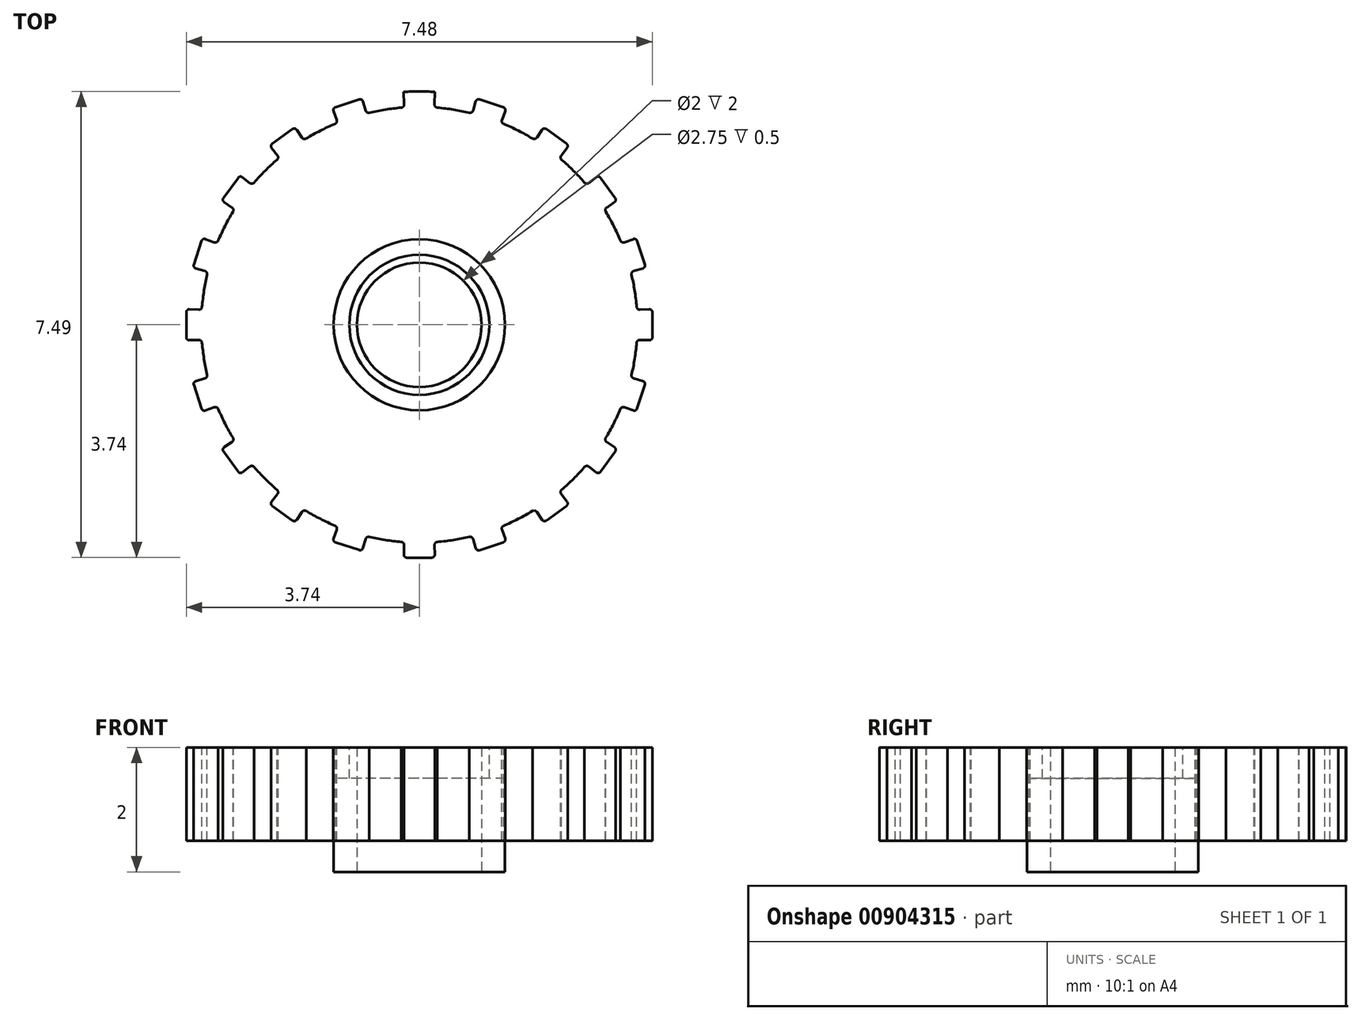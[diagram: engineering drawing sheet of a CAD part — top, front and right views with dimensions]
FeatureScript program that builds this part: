
annotation { "Feature Type Name" : "Feature", "Feature Type Description" : "" }
export const myFeature = defineFeature(function(context is Context, id is Id, definition is map)
    precondition{}
    {
        {
            var Q0;
            Q0=qCreatedBy(makeId("Front.planeOp"),FACE);
            var sketch = newSketch(context, id + "F0", { "sketchPlane" : qUnion([Q0])});
            skLineSegment(sketch, "E0.bottom", {"start": v(0, 0) * mm, "end": v(-3.75, 0) * mm});
            skLineSegment(sketch, "E0.top", {"start": v(0, 2) * mm, "end": v(-3.75, 2) * mm});
            skLineSegment(sketch, "E0.left", {"start": v(0, 0) * mm, "end": v(0, 2) * mm});
            skLineSegment(sketch, "E0.right", {"start": v(-3.75, 0) * mm, "end": v(-3.75, 2) * mm});
            skLineSegment(sketch, "E1", {"start": v(-1, 2) * mm, "end": v(-1, 0) * mm});
            skSolve(sketch);
        }
        {
            var Q0;
            {var subQ0=sQuery(id+"F0.wireOp",EDGE,"E0.right");Q0=makeQuery(id+"F0.imprint","IMPRINT",FACE,{"disambiguationData":[TD([[makeQuery(id+"F0.imprint","IMPRINT",EDGE,{"derivedFrom":subQ0}),-1.0]])]});}
            var Q1;
            Q1=sQuery(id+"F0.wireOp",EDGE,"E0.left");
            revolve(context, id + "F1", {"surfaceOperationType" : NewSurfaceOperationType.NEW, "entities" : qUnion([Q0]), "axis" : qUnion([Q1]), "revolveType" : RevolveType.FULL});
        }
        {
            var Q0;
            Q0=makeQuery(id+"F1.opRevolve","SWEPT_FACE",FACE,{"disambiguationData":[OSD([sQuery(id+"F0.wireOp",EDGE,"E0.top")])]});
            var sketch = newSketch(context, id + "F2", { "sketchPlane" : qUnion([Q0])});
            skLineSegment(sketch, "E2", {"start": v(0, 0) * mm, "end": v(0, 3.75) * mm});
            skLineSegment(sketch, "E3", {"start": v(0, 3.74) * mm, "end": v(-0.25, 3.74) * mm});
            skLineSegment(sketch, "E4", {"start": v(-0.25, 3.74) * mm, "end": v(0.25, 3.74) * mm});
            skLineSegment(sketch, "E5.bottom", {"start": v(0.12, 0) * mm, "end": v(-0.12, 0) * mm});
            skLineSegment(sketch, "E5.top", {"start": v(0.12, 0) * mm, "end": v(-0.12, 0) * mm});
            skLineSegment(sketch, "E5.left", {"start": v(0.12, 0) * mm, "end": v(0.12, 0) * mm});
            skLineSegment(sketch, "E5.right", {"start": v(-0.12, 0) * mm, "end": v(-0.12, 0) * mm});
            skPoint(sketch, "E5.middle", {"position": v(0, 0) * mm});
            skLineSegment(sketch, "E6", {"start": v(-0.25, 3.74) * mm, "end": v(-0.13, 0) * mm});
            skLineSegment(sketch, "E7", {"start": v(0.25, 3.74) * mm, "end": v(0.12, 0) * mm});
            skCircle(sketch, "E8", {"center": v(0, 0) * mm, "radius": 3.5 * mm});
            skLineSegment(sketch, "E9", {"start": v(-0.25, 3.74) * mm, "end": v(-0.2, 3.74) * mm});
            skLineSegment(sketch, "E10", {"start": v(-0.2, 3.74) * mm, "end": v(0.2, 3.74) * mm});
            skLineSegment(sketch, "E11", {"start": v(0.2, 3.74) * mm, "end": v(0.25, 3.74) * mm});
            skLineSegment(sketch, "E12", {"start": v(-0.2, 3.74) * mm, "end": v(-0.12, 0) * mm});
            skLineSegment(sketch, "E13", {"start": v(0.2, 3.74) * mm, "end": v(0.12, 0) * mm});
            skLineSegment(sketch, "E14", {"start": v(-0.25, 3.7) * mm, "end": v(0.25, 3.7) * mm});
            skLineSegment(sketch, "E15", {"start": v(-0.25, 3.7) * mm, "end": v(-0.3, 3.7) * mm});
            skLineSegment(sketch, "E16", {"start": v(0.25, 3.7) * mm, "end": v(0.3, 3.7) * mm});
            skLineSegment(sketch, "E17", {"start": v(-0.3, 3.7) * mm, "end": v(-0.13, 0) * mm});
            skLineSegment(sketch, "E18", {"start": v(0.3, 3.7) * mm, "end": v(0.13, 0) * mm});
            skLineSegment(sketch, "E19", {"start": v(-0.24, 3.54) * mm, "end": v(0.2, 3.54) * mm});
            skLineSegment(sketch, "E20", {"start": v(0.2, 3.54) * mm, "end": v(0.24, 3.54) * mm});
            skLineSegment(sketch, "E21", {"start": v(0.24, 3.54) * mm, "end": v(-0.2, 3.54) * mm});
            skArc(sketch, "E22", {"start": v(-0.29, 3.49) * mm, "mid": v(-0.26, 3.5) * mm, "end": v(-0.24, 3.54) * mm});
            skArc(sketch, "E23", {"start": v(-0.2, 3.74) * mm, "mid": v(-0.23, 3.73) * mm, "end": v(-0.25, 3.7) * mm});
            skArc(sketch, "E24", {"start": v(0.25, 3.7) * mm, "mid": v(0.23, 3.73) * mm, "end": v(0.2, 3.74) * mm});
            skArc(sketch, "E25", {"start": v(0.24, 3.54) * mm, "mid": v(0.26, 3.5) * mm, "end": v(0.29, 3.49) * mm});
            skArc(sketch, "E26.1.0", {"start": v(-1.35, 3.23) * mm, "mid": v(-1.33, 3.26) * mm, "end": v(-1.33, 3.3) * mm});
            skLineSegment(sketch, "E26.1.1", {"start": v(-1.4, 3.48) * mm, "end": v(-0.12, -0.04) * mm});
            skArc(sketch, "E26.1.2", {"start": v(-1.35, 3.5) * mm, "mid": v(-1.37, 3.47) * mm, "end": v(-1.38, 3.43) * mm});
            skLineSegment(sketch, "E26.1.3", {"start": v(-1.4, 3.48) * mm, "end": v(-0.92, 3.64) * mm});
            skArc(sketch, "E26.1.4", {"start": v(-0.9, 3.59) * mm, "mid": v(-0.93, 3.62) * mm, "end": v(-0.97, 3.62) * mm});
            skLineSegment(sketch, "E26.1.5", {"start": v(-0.92, 3.64) * mm, "end": v(0.12, 0.04) * mm});
            skArc(sketch, "E26.1.6", {"start": v(-0.86, 3.44) * mm, "mid": v(-0.84, 3.41) * mm, "end": v(-0.8, 3.4) * mm});
            skArc(sketch, "E26.2.0", {"start": v(-2.28, 2.65) * mm, "mid": v(-2.27, 2.69) * mm, "end": v(-2.28, 2.72) * mm});
            skLineSegment(sketch, "E26.2.1", {"start": v(-2.4, 2.88) * mm, "end": v(-0.1, -0.07) * mm});
            skArc(sketch, "E26.2.2", {"start": v(-2.36, 2.9) * mm, "mid": v(-2.38, 2.88) * mm, "end": v(-2.37, 2.84) * mm});
            skLineSegment(sketch, "E26.2.3", {"start": v(-2.4, 2.88) * mm, "end": v(-2, 3.17) * mm});
            skArc(sketch, "E26.2.4", {"start": v(-1.97, 3.13) * mm, "mid": v(-2, 3.15) * mm, "end": v(-2.04, 3.14) * mm});
            skLineSegment(sketch, "E26.2.5", {"start": v(-2, 3.17) * mm, "end": v(0.1, 0.07) * mm});
            skArc(sketch, "E26.2.6", {"start": v(-1.88, 3) * mm, "mid": v(-1.85, 2.99) * mm, "end": v(-1.82, 3) * mm});
            skArc(sketch, "E27.2.3.0", {"start": v(-3, 1.82) * mm, "mid": v(-2.99, 1.85) * mm, "end": v(-3, 1.88) * mm});
            skLineSegment(sketch, "E27.4.3.0", {"start": v(-3.17, 2) * mm, "end": v(-0.07, -0.1) * mm});
            skArc(sketch, "E27.7.3.0", {"start": v(-3.14, 2.04) * mm, "mid": v(-3.15, 2) * mm, "end": v(-3.13, 1.97) * mm});
            skLineSegment(sketch, "E27.11.3.0", {"start": v(-3.17, 2) * mm, "end": v(-2.88, 2.4) * mm});
            skArc(sketch, "E27.14.3.0", {"start": v(-2.84, 2.37) * mm, "mid": v(-2.88, 2.38) * mm, "end": v(-2.9, 2.36) * mm});
            skLineSegment(sketch, "E27.18.3.0", {"start": v(-2.88, 2.4) * mm, "end": v(0.07, 0.1) * mm});
            skArc(sketch, "E27.21.3.0", {"start": v(-2.72, 2.28) * mm, "mid": v(-2.69, 2.27) * mm, "end": v(-2.65, 2.28) * mm});
            skArc(sketch, "E27.2.4.0", {"start": v(-3.4, 0.8) * mm, "mid": v(-3.41, 0.84) * mm, "end": v(-3.44, 0.86) * mm});
            skLineSegment(sketch, "E27.4.4.0", {"start": v(-3.64, 0.92) * mm, "end": v(-0.04, -0.12) * mm});
            skArc(sketch, "E27.7.4.0", {"start": v(-3.62, 0.97) * mm, "mid": v(-3.62, 0.93) * mm, "end": v(-3.59, 0.9) * mm});
            skLineSegment(sketch, "E27.11.4.0", {"start": v(-3.64, 0.92) * mm, "end": v(-3.48, 1.4) * mm});
            skArc(sketch, "E27.14.4.0", {"start": v(-3.43, 1.38) * mm, "mid": v(-3.47, 1.37) * mm, "end": v(-3.5, 1.35) * mm});
            skLineSegment(sketch, "E27.18.4.0", {"start": v(-3.48, 1.4) * mm, "end": v(0.04, 0.12) * mm});
            skArc(sketch, "E27.21.4.0", {"start": v(-3.3, 1.33) * mm, "mid": v(-3.26, 1.33) * mm, "end": v(-3.23, 1.35) * mm});
            skArc(sketch, "E27.2.5.0", {"start": v(-3.49, -0.29) * mm, "mid": v(-3.5, -0.26) * mm, "end": v(-3.54, -0.24) * mm});
            skLineSegment(sketch, "E27.4.5.0", {"start": v(-3.74, -0.25) * mm, "end": v(0, -0.12) * mm});
            skArc(sketch, "E27.7.5.0", {"start": v(-3.74, -0.2) * mm, "mid": v(-3.73, -0.23) * mm, "end": v(-3.7, -0.25) * mm});
            skLineSegment(sketch, "E27.11.5.0", {"start": v(-3.74, -0.25) * mm, "end": v(-3.74, 0.25) * mm});
            skArc(sketch, "E27.14.5.0", {"start": v(-3.7, 0.25) * mm, "mid": v(-3.73, 0.23) * mm, "end": v(-3.74, 0.2) * mm});
            skLineSegment(sketch, "E27.18.5.0", {"start": v(-3.74, 0.25) * mm, "end": v(0, 0.13) * mm});
            skArc(sketch, "E27.21.5.0", {"start": v(-3.54, 0.24) * mm, "mid": v(-3.5, 0.26) * mm, "end": v(-3.49, 0.29) * mm});
            skArc(sketch, "E27.2.6.0", {"start": v(-3.23, -1.35) * mm, "mid": v(-3.26, -1.33) * mm, "end": v(-3.3, -1.33) * mm});
            skLineSegment(sketch, "E27.4.6.0", {"start": v(-3.48, -1.4) * mm, "end": v(0.04, -0.12) * mm});
            skArc(sketch, "E27.7.6.0", {"start": v(-3.5, -1.35) * mm, "mid": v(-3.47, -1.37) * mm, "end": v(-3.43, -1.38) * mm});
            skLineSegment(sketch, "E27.11.6.0", {"start": v(-3.48, -1.4) * mm, "end": v(-3.64, -0.92) * mm});
            skArc(sketch, "E27.14.6.0", {"start": v(-3.59, -0.9) * mm, "mid": v(-3.62, -0.93) * mm, "end": v(-3.62, -0.97) * mm});
            skLineSegment(sketch, "E27.18.6.0", {"start": v(-3.64, -0.92) * mm, "end": v(-0.04, 0.12) * mm});
            skArc(sketch, "E27.21.6.0", {"start": v(-3.44, -0.86) * mm, "mid": v(-3.41, -0.84) * mm, "end": v(-3.4, -0.8) * mm});
            skArc(sketch, "E27.2.7.0", {"start": v(-2.65, -2.28) * mm, "mid": v(-2.69, -2.27) * mm, "end": v(-2.72, -2.28) * mm});
            skLineSegment(sketch, "E27.4.7.0", {"start": v(-2.88, -2.4) * mm, "end": v(0.07, -0.1) * mm});
            skArc(sketch, "E27.7.7.0", {"start": v(-2.9, -2.36) * mm, "mid": v(-2.88, -2.38) * mm, "end": v(-2.84, -2.37) * mm});
            skLineSegment(sketch, "E27.11.7.0", {"start": v(-2.88, -2.4) * mm, "end": v(-3.17, -2) * mm});
            skArc(sketch, "E27.14.7.0", {"start": v(-3.13, -1.97) * mm, "mid": v(-3.15, -2) * mm, "end": v(-3.14, -2.04) * mm});
            skLineSegment(sketch, "E27.18.7.0", {"start": v(-3.17, -2) * mm, "end": v(-0.07, 0.1) * mm});
            skArc(sketch, "E27.21.7.0", {"start": v(-3, -1.88) * mm, "mid": v(-2.99, -1.85) * mm, "end": v(-3, -1.82) * mm});
            skArc(sketch, "E28.2.8.0", {"start": v(-1.82, -3) * mm, "mid": v(-1.85, -2.99) * mm, "end": v(-1.88, -3) * mm});
            skLineSegment(sketch, "E28.4.8.0", {"start": v(-2, -3.17) * mm, "end": v(0.1, -0.07) * mm});
            skArc(sketch, "E28.7.8.0", {"start": v(-2.04, -3.14) * mm, "mid": v(-2, -3.15) * mm, "end": v(-1.97, -3.13) * mm});
            skLineSegment(sketch, "E28.11.8.0", {"start": v(-2, -3.17) * mm, "end": v(-2.4, -2.88) * mm});
            skArc(sketch, "E28.14.8.0", {"start": v(-2.37, -2.84) * mm, "mid": v(-2.38, -2.88) * mm, "end": v(-2.36, -2.9) * mm});
            skLineSegment(sketch, "E28.18.8.0", {"start": v(-2.4, -2.88) * mm, "end": v(-0.1, 0.07) * mm});
            skArc(sketch, "E28.21.8.0", {"start": v(-2.28, -2.72) * mm, "mid": v(-2.27, -2.69) * mm, "end": v(-2.28, -2.65) * mm});
            skArc(sketch, "E28.2.9.0", {"start": v(-0.8, -3.4) * mm, "mid": v(-0.84, -3.41) * mm, "end": v(-0.86, -3.44) * mm});
            skLineSegment(sketch, "E28.4.9.0", {"start": v(-0.92, -3.64) * mm, "end": v(0.12, -0.04) * mm});
            skArc(sketch, "E28.7.9.0", {"start": v(-0.97, -3.62) * mm, "mid": v(-0.93, -3.62) * mm, "end": v(-0.9, -3.59) * mm});
            skLineSegment(sketch, "E28.11.9.0", {"start": v(-0.92, -3.64) * mm, "end": v(-1.4, -3.48) * mm});
            skArc(sketch, "E28.14.9.0", {"start": v(-1.38, -3.43) * mm, "mid": v(-1.37, -3.47) * mm, "end": v(-1.35, -3.5) * mm});
            skLineSegment(sketch, "E28.18.9.0", {"start": v(-1.4, -3.48) * mm, "end": v(-0.12, 0.04) * mm});
            skArc(sketch, "E28.21.9.0", {"start": v(-1.33, -3.3) * mm, "mid": v(-1.33, -3.26) * mm, "end": v(-1.35, -3.23) * mm});
            skArc(sketch, "E28.2.10.0", {"start": v(0.29, -3.49) * mm, "mid": v(0.26, -3.5) * mm, "end": v(0.24, -3.54) * mm});
            skLineSegment(sketch, "E28.4.10.0", {"start": v(0.25, -3.74) * mm, "end": v(0.13, 0) * mm});
            skArc(sketch, "E28.7.10.0", {"start": v(0.2, -3.74) * mm, "mid": v(0.23, -3.73) * mm, "end": v(0.25, -3.7) * mm});
            skLineSegment(sketch, "E28.11.10.0", {"start": v(0.25, -3.74) * mm, "end": v(-0.25, -3.74) * mm});
            skArc(sketch, "E28.14.10.0", {"start": v(-0.25, -3.7) * mm, "mid": v(-0.23, -3.73) * mm, "end": v(-0.2, -3.74) * mm});
            skLineSegment(sketch, "E28.18.10.0", {"start": v(-0.25, -3.74) * mm, "end": v(-0.12, 0) * mm});
            skArc(sketch, "E28.21.10.0", {"start": v(-0.24, -3.54) * mm, "mid": v(-0.26, -3.5) * mm, "end": v(-0.29, -3.49) * mm});
            skArc(sketch, "E28.2.11.0", {"start": v(1.35, -3.23) * mm, "mid": v(1.33, -3.26) * mm, "end": v(1.33, -3.3) * mm});
            skLineSegment(sketch, "E28.4.11.0", {"start": v(1.4, -3.48) * mm, "end": v(0.12, 0.04) * mm});
            skArc(sketch, "E28.7.11.0", {"start": v(1.35, -3.5) * mm, "mid": v(1.37, -3.47) * mm, "end": v(1.38, -3.43) * mm});
            skLineSegment(sketch, "E28.11.11.0", {"start": v(1.4, -3.48) * mm, "end": v(0.92, -3.64) * mm});
            skArc(sketch, "E28.14.11.0", {"start": v(0.9, -3.59) * mm, "mid": v(0.93, -3.62) * mm, "end": v(0.97, -3.62) * mm});
            skLineSegment(sketch, "E28.18.11.0", {"start": v(0.92, -3.64) * mm, "end": v(-0.12, -0.04) * mm});
            skArc(sketch, "E28.21.11.0", {"start": v(0.86, -3.44) * mm, "mid": v(0.84, -3.41) * mm, "end": v(0.8, -3.4) * mm});
            skArc(sketch, "E28.2.12.0", {"start": v(2.28, -2.65) * mm, "mid": v(2.27, -2.69) * mm, "end": v(2.28, -2.72) * mm});
            skLineSegment(sketch, "E28.4.12.0", {"start": v(2.4, -2.88) * mm, "end": v(0.1, 0.07) * mm});
            skArc(sketch, "E28.7.12.0", {"start": v(2.36, -2.9) * mm, "mid": v(2.38, -2.88) * mm, "end": v(2.37, -2.84) * mm});
            skLineSegment(sketch, "E28.11.12.0", {"start": v(2.4, -2.88) * mm, "end": v(2, -3.17) * mm});
            skArc(sketch, "E28.14.12.0", {"start": v(1.97, -3.13) * mm, "mid": v(2, -3.15) * mm, "end": v(2.04, -3.14) * mm});
            skLineSegment(sketch, "E28.18.12.0", {"start": v(2, -3.17) * mm, "end": v(-0.1, -0.07) * mm});
            skArc(sketch, "E28.21.12.0", {"start": v(1.88, -3) * mm, "mid": v(1.85, -2.99) * mm, "end": v(1.82, -3) * mm});
            skArc(sketch, "E28.2.13.0", {"start": v(3, -1.82) * mm, "mid": v(2.99, -1.85) * mm, "end": v(3, -1.88) * mm});
            skLineSegment(sketch, "E28.4.13.0", {"start": v(3.17, -2) * mm, "end": v(0.07, 0.1) * mm});
            skArc(sketch, "E28.7.13.0", {"start": v(3.14, -2.04) * mm, "mid": v(3.15, -2) * mm, "end": v(3.13, -1.97) * mm});
            skLineSegment(sketch, "E28.11.13.0", {"start": v(3.17, -2) * mm, "end": v(2.88, -2.4) * mm});
            skArc(sketch, "E28.14.13.0", {"start": v(2.84, -2.37) * mm, "mid": v(2.88, -2.38) * mm, "end": v(2.9, -2.36) * mm});
            skLineSegment(sketch, "E28.18.13.0", {"start": v(2.88, -2.4) * mm, "end": v(-0.07, -0.1) * mm});
            skArc(sketch, "E28.21.13.0", {"start": v(2.72, -2.28) * mm, "mid": v(2.69, -2.27) * mm, "end": v(2.65, -2.28) * mm});
            skArc(sketch, "E29.2.14.0", {"start": v(3.4, -0.8) * mm, "mid": v(3.41, -0.84) * mm, "end": v(3.44, -0.86) * mm});
            skLineSegment(sketch, "E29.4.14.0", {"start": v(3.64, -0.92) * mm, "end": v(0.04, 0.12) * mm});
            skArc(sketch, "E29.7.14.0", {"start": v(3.62, -0.97) * mm, "mid": v(3.62, -0.93) * mm, "end": v(3.59, -0.9) * mm});
            skLineSegment(sketch, "E29.11.14.0", {"start": v(3.64, -0.92) * mm, "end": v(3.48, -1.4) * mm});
            skArc(sketch, "E29.14.14.0", {"start": v(3.43, -1.38) * mm, "mid": v(3.47, -1.37) * mm, "end": v(3.5, -1.35) * mm});
            skLineSegment(sketch, "E29.18.14.0", {"start": v(3.48, -1.4) * mm, "end": v(-0.04, -0.12) * mm});
            skArc(sketch, "E29.21.14.0", {"start": v(3.3, -1.33) * mm, "mid": v(3.26, -1.33) * mm, "end": v(3.23, -1.35) * mm});
            skArc(sketch, "E29.2.15.0", {"start": v(3.49, 0.29) * mm, "mid": v(3.5, 0.26) * mm, "end": v(3.54, 0.24) * mm});
            skLineSegment(sketch, "E29.4.15.0", {"start": v(3.74, 0.25) * mm, "end": v(0, 0.12) * mm});
            skArc(sketch, "E29.7.15.0", {"start": v(3.74, 0.2) * mm, "mid": v(3.73, 0.23) * mm, "end": v(3.7, 0.25) * mm});
            skLineSegment(sketch, "E29.11.15.0", {"start": v(3.74, 0.25) * mm, "end": v(3.74, -0.25) * mm});
            skArc(sketch, "E29.14.15.0", {"start": v(3.7, -0.25) * mm, "mid": v(3.73, -0.23) * mm, "end": v(3.74, -0.2) * mm});
            skLineSegment(sketch, "E29.18.15.0", {"start": v(3.74, -0.25) * mm, "end": v(0, -0.13) * mm});
            skArc(sketch, "E29.21.15.0", {"start": v(3.54, -0.24) * mm, "mid": v(3.5, -0.26) * mm, "end": v(3.49, -0.29) * mm});
            skArc(sketch, "E30.2.16.0", {"start": v(3.23, 1.35) * mm, "mid": v(3.26, 1.33) * mm, "end": v(3.3, 1.33) * mm});
            skLineSegment(sketch, "E30.4.16.0", {"start": v(3.48, 1.4) * mm, "end": v(-0.04, 0.12) * mm});
            skArc(sketch, "E30.7.16.0", {"start": v(3.5, 1.35) * mm, "mid": v(3.47, 1.37) * mm, "end": v(3.43, 1.38) * mm});
            skLineSegment(sketch, "E30.11.16.0", {"start": v(3.48, 1.4) * mm, "end": v(3.64, 0.92) * mm});
            skArc(sketch, "E30.14.16.0", {"start": v(3.59, 0.9) * mm, "mid": v(3.62, 0.93) * mm, "end": v(3.62, 0.97) * mm});
            skLineSegment(sketch, "E30.18.16.0", {"start": v(3.64, 0.92) * mm, "end": v(0.04, -0.12) * mm});
            skArc(sketch, "E30.21.16.0", {"start": v(3.44, 0.86) * mm, "mid": v(3.41, 0.84) * mm, "end": v(3.4, 0.8) * mm});
            skArc(sketch, "E30.2.17.0", {"start": v(2.65, 2.28) * mm, "mid": v(2.69, 2.27) * mm, "end": v(2.72, 2.28) * mm});
            skLineSegment(sketch, "E30.4.17.0", {"start": v(2.88, 2.4) * mm, "end": v(-0.07, 0.1) * mm});
            skArc(sketch, "E30.7.17.0", {"start": v(2.9, 2.36) * mm, "mid": v(2.88, 2.38) * mm, "end": v(2.84, 2.37) * mm});
            skLineSegment(sketch, "E30.11.17.0", {"start": v(2.88, 2.4) * mm, "end": v(3.17, 2) * mm});
            skArc(sketch, "E30.14.17.0", {"start": v(3.13, 1.97) * mm, "mid": v(3.15, 2) * mm, "end": v(3.14, 2.04) * mm});
            skLineSegment(sketch, "E30.18.17.0", {"start": v(3.17, 2) * mm, "end": v(0.07, -0.1) * mm});
            skArc(sketch, "E30.21.17.0", {"start": v(3, 1.88) * mm, "mid": v(2.99, 1.85) * mm, "end": v(3, 1.82) * mm});
            skArc(sketch, "E30.2.18.0", {"start": v(1.82, 3) * mm, "mid": v(1.85, 2.99) * mm, "end": v(1.88, 3) * mm});
            skLineSegment(sketch, "E30.4.18.0", {"start": v(2, 3.17) * mm, "end": v(-0.1, 0.07) * mm});
            skArc(sketch, "E30.7.18.0", {"start": v(2.04, 3.14) * mm, "mid": v(2, 3.15) * mm, "end": v(1.97, 3.13) * mm});
            skLineSegment(sketch, "E30.11.18.0", {"start": v(2, 3.17) * mm, "end": v(2.4, 2.88) * mm});
            skArc(sketch, "E30.14.18.0", {"start": v(2.37, 2.84) * mm, "mid": v(2.38, 2.88) * mm, "end": v(2.36, 2.9) * mm});
            skLineSegment(sketch, "E30.18.18.0", {"start": v(2.4, 2.88) * mm, "end": v(0.1, -0.07) * mm});
            skArc(sketch, "E30.21.18.0", {"start": v(2.28, 2.72) * mm, "mid": v(2.27, 2.69) * mm, "end": v(2.28, 2.65) * mm});
            skArc(sketch, "E30.2.19.0", {"start": v(0.8, 3.4) * mm, "mid": v(0.84, 3.41) * mm, "end": v(0.86, 3.44) * mm});
            skLineSegment(sketch, "E30.4.19.0", {"start": v(0.92, 3.64) * mm, "end": v(-0.12, 0.04) * mm});
            skArc(sketch, "E30.7.19.0", {"start": v(0.97, 3.62) * mm, "mid": v(0.93, 3.62) * mm, "end": v(0.9, 3.59) * mm});
            skLineSegment(sketch, "E30.11.19.0", {"start": v(0.92, 3.64) * mm, "end": v(1.4, 3.48) * mm});
            skArc(sketch, "E30.14.19.0", {"start": v(1.38, 3.43) * mm, "mid": v(1.37, 3.47) * mm, "end": v(1.35, 3.5) * mm});
            skLineSegment(sketch, "E30.18.19.0", {"start": v(1.4, 3.48) * mm, "end": v(0.12, -0.04) * mm});
            skArc(sketch, "E30.21.19.0", {"start": v(1.33, 3.3) * mm, "mid": v(1.33, 3.26) * mm, "end": v(1.35, 3.23) * mm});
            skSolve(sketch);
        }
        {
            var Q0;
            {var subQ1=sQuery(id+"F2.wireOp",EDGE,"E15");Q0=makeQuery(id+"F2.imprint","IMPRINT",FACE,{"disambiguationData":[TD([[makeQuery(id+"F2.imprint","IMPRINT",EDGE,{"derivedFrom":subQ1}),-1.0]])]});}
            var Q1;
            {var subQ0=sQuery(id+"F2.wireOp",EDGE,"E15");Q1=makeQuery(id+"F2.imprint","IMPRINT",FACE,{"disambiguationData":[TD([[makeQuery(id+"F2.imprint","IMPRINT",EDGE,{"derivedFrom":subQ0}),1.0]])]});}
            var Q2;
            {var subQ0=sQuery(id+"F2.wireOp",EDGE,"E9");Q2=makeQuery(id+"F2.imprint","IMPRINT",FACE,{"disambiguationData":[TD([[makeQuery(id+"F2.imprint","IMPRINT",EDGE,{"derivedFrom":subQ0}),-1.0]])]});}
            var Q3;
            {var subQ5=sQuery(id+"F2.wireOp",EDGE,"E9");Q3=makeQuery(id+"F2.imprint","IMPRINT",FACE,{"disambiguationData":[TD([[makeQuery(id+"F2.imprint","IMPRINT",EDGE,{"derivedFrom":subQ5}),1.0]])]});}
            var Q4;
            {var subQ5=sQuery(id+"F2.wireOp",EDGE,"E11");Q4=makeQuery(id+"F2.imprint","IMPRINT",FACE,{"disambiguationData":[TD([[makeQuery(id+"F2.imprint","IMPRINT",EDGE,{"derivedFrom":subQ5}),1.0]])]});}
            var Q5;
            {var subQ0=sQuery(id+"F2.wireOp",EDGE,"E11");Q5=makeQuery(id+"F2.imprint","IMPRINT",FACE,{"disambiguationData":[TD([[makeQuery(id+"F2.imprint","IMPRINT",EDGE,{"derivedFrom":subQ0}),-1.0]])]});}
            var Q6;
            {var subQ0=sQuery(id+"F2.wireOp",EDGE,"E16");Q6=makeQuery(id+"F2.imprint","IMPRINT",FACE,{"disambiguationData":[TD([[makeQuery(id+"F2.imprint","IMPRINT",EDGE,{"derivedFrom":subQ0}),1.0]])]});}
            var Q7;
            {var subQ0=sQuery(id+"F2.wireOp",EDGE,"E16");Q7=makeQuery(id+"F2.imprint","IMPRINT",FACE,{"disambiguationData":[TD([[makeQuery(id+"F2.imprint","IMPRINT",EDGE,{"derivedFrom":subQ0}),-1.0]])]});}
            var Q8;
            {var subQ3=sQuery(id+"F2.wireOp",EDGE,"E27.7.7.0");Q8=makeQuery(id+"F2.imprint","IMPRINT",FACE,{"disambiguationData":[TD([[makeQuery(id+"F2.imprint","IMPRINT",EDGE,{"derivedFrom":subQ3}),-1.0]])]});}
            var Q9;
            {var subQ0=sQuery(id+"F2.wireOp",EDGE,"E27.11.7.0");var subQ3=makeQuery(id+"F2.imprint","INTERSECT",VERTEX,{"derivedFrom":[sQuery(id+"F2.wireOp",EDGE,"E27.7.7.0"),subQ0]});Q9=makeQuery(id+"F2.imprint","IMPRINT",FACE,{"disambiguationData":[TD([[makeQuery(id+"F2.imprint","IMPRINT",EDGE,{"disambiguationData":[TD([[subQ3,-1.0]])],"derivedFrom":subQ0}),1.0]])]});}
            var Q10;
            {var subQ3=sQuery(id+"F2.wireOp",EDGE,"E27.14.7.0");Q10=makeQuery(id+"F2.imprint","IMPRINT",FACE,{"disambiguationData":[TD([[makeQuery(id+"F2.imprint","IMPRINT",EDGE,{"derivedFrom":subQ3}),-1.0]])]});}
            var Q11;
            {var subQ4=sQuery(id+"F2.wireOp",EDGE,"E27.2.6.0");Q11=makeQuery(id+"F2.imprint","IMPRINT",FACE,{"disambiguationData":[TD([[makeQuery(id+"F2.imprint","IMPRINT",EDGE,{"derivedFrom":subQ4}),1.0]])]});}
            var Q12;
            {var subQ3=sQuery(id+"F2.wireOp",EDGE,"E27.7.6.0");Q12=makeQuery(id+"F2.imprint","IMPRINT",FACE,{"disambiguationData":[TD([[makeQuery(id+"F2.imprint","IMPRINT",EDGE,{"derivedFrom":subQ3}),-1.0]])]});}
            var Q13;
            {var subQ0=sQuery(id+"F2.wireOp",EDGE,"E27.11.6.0");var subQ3=makeQuery(id+"F2.imprint","INTERSECT",VERTEX,{"derivedFrom":[sQuery(id+"F2.wireOp",EDGE,"E27.7.6.0"),subQ0]});Q13=makeQuery(id+"F2.imprint","IMPRINT",FACE,{"disambiguationData":[TD([[makeQuery(id+"F2.imprint","IMPRINT",EDGE,{"disambiguationData":[TD([[subQ3,-1.0]])],"derivedFrom":subQ0}),1.0]])]});}
            var Q14;
            {var subQ1=sQuery(id+"F2.wireOp",EDGE,"E27.2.5.0");Q14=makeQuery(id+"F2.imprint","IMPRINT",FACE,{"disambiguationData":[TD([[makeQuery(id+"F2.imprint","IMPRINT",EDGE,{"derivedFrom":subQ1}),1.0]])]});}
            var Q15;
            {var subQ3=sQuery(id+"F2.wireOp",EDGE,"E27.14.6.0");Q15=makeQuery(id+"F2.imprint","IMPRINT",FACE,{"disambiguationData":[TD([[makeQuery(id+"F2.imprint","IMPRINT",EDGE,{"derivedFrom":subQ3}),-1.0]])]});}
            var Q16;
            {var subQ0=sQuery(id+"F2.wireOp",EDGE,"E27.11.5.0");var subQ3=makeQuery(id+"F2.imprint","INTERSECT",VERTEX,{"derivedFrom":[sQuery(id+"F2.wireOp",EDGE,"E27.7.5.0"),subQ0]});Q16=makeQuery(id+"F2.imprint","IMPRINT",FACE,{"disambiguationData":[TD([[makeQuery(id+"F2.imprint","IMPRINT",EDGE,{"disambiguationData":[TD([[subQ3,-1.0]])],"derivedFrom":subQ0}),1.0]])]});}
            var Q17;
            {var subQ3=sQuery(id+"F2.wireOp",EDGE,"E27.7.5.0");Q17=makeQuery(id+"F2.imprint","IMPRINT",FACE,{"disambiguationData":[TD([[makeQuery(id+"F2.imprint","IMPRINT",EDGE,{"derivedFrom":subQ3}),-1.0]])]});}
            var Q18;
            {var subQ3=sQuery(id+"F2.wireOp",EDGE,"E27.14.5.0");Q18=makeQuery(id+"F2.imprint","IMPRINT",FACE,{"disambiguationData":[TD([[makeQuery(id+"F2.imprint","IMPRINT",EDGE,{"derivedFrom":subQ3}),-1.0]])]});}
            var Q19;
            {var subQ4=sQuery(id+"F2.wireOp",EDGE,"E27.2.4.0");Q19=makeQuery(id+"F2.imprint","IMPRINT",FACE,{"disambiguationData":[TD([[makeQuery(id+"F2.imprint","IMPRINT",EDGE,{"derivedFrom":subQ4}),1.0]])]});}
            var Q20;
            {var subQ3=sQuery(id+"F2.wireOp",EDGE,"E27.7.4.0");Q20=makeQuery(id+"F2.imprint","IMPRINT",FACE,{"disambiguationData":[TD([[makeQuery(id+"F2.imprint","IMPRINT",EDGE,{"derivedFrom":subQ3}),-1.0]])]});}
            var Q21;
            {var subQ0=sQuery(id+"F2.wireOp",EDGE,"E27.11.4.0");var subQ3=makeQuery(id+"F2.imprint","INTERSECT",VERTEX,{"derivedFrom":[sQuery(id+"F2.wireOp",EDGE,"E27.7.4.0"),subQ0]});Q21=makeQuery(id+"F2.imprint","IMPRINT",FACE,{"disambiguationData":[TD([[makeQuery(id+"F2.imprint","IMPRINT",EDGE,{"disambiguationData":[TD([[subQ3,-1.0]])],"derivedFrom":subQ0}),1.0]])]});}
            var Q22;
            {var subQ3=sQuery(id+"F2.wireOp",EDGE,"E27.14.4.0");Q22=makeQuery(id+"F2.imprint","IMPRINT",FACE,{"disambiguationData":[TD([[makeQuery(id+"F2.imprint","IMPRINT",EDGE,{"derivedFrom":subQ3}),-1.0]])]});}
            var Q23;
            {var subQ1=sQuery(id+"F2.wireOp",EDGE,"E27.2.3.0");Q23=makeQuery(id+"F2.imprint","IMPRINT",FACE,{"disambiguationData":[TD([[makeQuery(id+"F2.imprint","IMPRINT",EDGE,{"derivedFrom":subQ1}),1.0]])]});}
            var Q24;
            {var subQ3=sQuery(id+"F2.wireOp",EDGE,"E27.7.3.0");Q24=makeQuery(id+"F2.imprint","IMPRINT",FACE,{"disambiguationData":[TD([[makeQuery(id+"F2.imprint","IMPRINT",EDGE,{"derivedFrom":subQ3}),-1.0]])]});}
            var Q25;
            {var subQ0=sQuery(id+"F2.wireOp",EDGE,"E27.11.3.0");var subQ3=makeQuery(id+"F2.imprint","INTERSECT",VERTEX,{"derivedFrom":[sQuery(id+"F2.wireOp",EDGE,"E27.7.3.0"),subQ0]});Q25=makeQuery(id+"F2.imprint","IMPRINT",FACE,{"disambiguationData":[TD([[makeQuery(id+"F2.imprint","IMPRINT",EDGE,{"disambiguationData":[TD([[subQ3,-1.0]])],"derivedFrom":subQ0}),1.0]])]});}
            var Q26;
            {var subQ3=sQuery(id+"F2.wireOp",EDGE,"E27.14.3.0");Q26=makeQuery(id+"F2.imprint","IMPRINT",FACE,{"disambiguationData":[TD([[makeQuery(id+"F2.imprint","IMPRINT",EDGE,{"derivedFrom":subQ3}),-1.0]])]});}
            var Q27;
            {var subQ0=sQuery(id+"F2.wireOp",EDGE,"E26.2.3");var subQ3=makeQuery(id+"F2.imprint","INTERSECT",VERTEX,{"derivedFrom":[sQuery(id+"F2.wireOp",EDGE,"E26.2.2"),subQ0]});Q27=makeQuery(id+"F2.imprint","IMPRINT",FACE,{"disambiguationData":[TD([[makeQuery(id+"F2.imprint","IMPRINT",EDGE,{"disambiguationData":[TD([[subQ3,-1.0]])],"derivedFrom":subQ0}),1.0]])]});}
            var Q28;
            {var subQ3=sQuery(id+"F2.wireOp",EDGE,"E26.2.2");Q28=makeQuery(id+"F2.imprint","IMPRINT",FACE,{"disambiguationData":[TD([[makeQuery(id+"F2.imprint","IMPRINT",EDGE,{"derivedFrom":subQ3}),-1.0]])]});}
            var Q29;
            {var subQ1=sQuery(id+"F2.wireOp",EDGE,"E26.2.0");Q29=makeQuery(id+"F2.imprint","IMPRINT",FACE,{"disambiguationData":[TD([[makeQuery(id+"F2.imprint","IMPRINT",EDGE,{"derivedFrom":subQ1}),1.0]])]});}
            var Q30;
            {var subQ3=sQuery(id+"F2.wireOp",EDGE,"E26.2.4");Q30=makeQuery(id+"F2.imprint","IMPRINT",FACE,{"disambiguationData":[TD([[makeQuery(id+"F2.imprint","IMPRINT",EDGE,{"derivedFrom":subQ3}),-1.0]])]});}
            var Q31;
            {var subQ1=sQuery(id+"F2.wireOp",EDGE,"E26.1.0");Q31=makeQuery(id+"F2.imprint","IMPRINT",FACE,{"disambiguationData":[TD([[makeQuery(id+"F2.imprint","IMPRINT",EDGE,{"derivedFrom":subQ1}),1.0]])]});}
            var Q32;
            {var subQ3=sQuery(id+"F2.wireOp",EDGE,"E26.1.2");Q32=makeQuery(id+"F2.imprint","IMPRINT",FACE,{"disambiguationData":[TD([[makeQuery(id+"F2.imprint","IMPRINT",EDGE,{"derivedFrom":subQ3}),-1.0]])]});}
            var Q33;
            {var subQ3=sQuery(id+"F2.wireOp",EDGE,"E26.1.4");Q33=makeQuery(id+"F2.imprint","IMPRINT",FACE,{"disambiguationData":[TD([[makeQuery(id+"F2.imprint","IMPRINT",EDGE,{"derivedFrom":subQ3}),-1.0]])]});}
            var Q34;
            {var subQ0=sQuery(id+"F2.wireOp",EDGE,"E26.1.3");var subQ3=makeQuery(id+"F2.imprint","INTERSECT",VERTEX,{"derivedFrom":[sQuery(id+"F2.wireOp",EDGE,"E26.1.2"),subQ0]});Q34=makeQuery(id+"F2.imprint","IMPRINT",FACE,{"disambiguationData":[TD([[makeQuery(id+"F2.imprint","IMPRINT",EDGE,{"disambiguationData":[TD([[subQ3,-1.0]])],"derivedFrom":subQ0}),1.0]])]});}
            var Q35;
            {var subQ3=sQuery(id+"F2.wireOp",EDGE,"E28.7.13.0");Q35=makeQuery(id+"F2.imprint","IMPRINT",FACE,{"disambiguationData":[TD([[makeQuery(id+"F2.imprint","IMPRINT",EDGE,{"derivedFrom":subQ3}),-1.0]])]});}
            var Q36;
            {var subQ0=sQuery(id+"F2.wireOp",EDGE,"E28.11.13.0");var subQ3=makeQuery(id+"F2.imprint","INTERSECT",VERTEX,{"derivedFrom":[sQuery(id+"F2.wireOp",EDGE,"E28.7.13.0"),subQ0]});Q36=makeQuery(id+"F2.imprint","IMPRINT",FACE,{"disambiguationData":[TD([[makeQuery(id+"F2.imprint","IMPRINT",EDGE,{"disambiguationData":[TD([[subQ3,-1.0]])],"derivedFrom":subQ0}),1.0]])]});}
            var Q37;
            {var subQ3=sQuery(id+"F2.wireOp",EDGE,"E28.14.13.0");Q37=makeQuery(id+"F2.imprint","IMPRINT",FACE,{"disambiguationData":[TD([[makeQuery(id+"F2.imprint","IMPRINT",EDGE,{"derivedFrom":subQ3}),-1.0]])]});}
            var Q38;
            {var subQ1=sQuery(id+"F2.wireOp",EDGE,"E28.2.12.0");Q38=makeQuery(id+"F2.imprint","IMPRINT",FACE,{"disambiguationData":[TD([[makeQuery(id+"F2.imprint","IMPRINT",EDGE,{"derivedFrom":subQ1}),1.0]])]});}
            var Q39;
            {var subQ3=sQuery(id+"F2.wireOp",EDGE,"E28.7.12.0");Q39=makeQuery(id+"F2.imprint","IMPRINT",FACE,{"disambiguationData":[TD([[makeQuery(id+"F2.imprint","IMPRINT",EDGE,{"derivedFrom":subQ3}),-1.0]])]});}
            var Q40;
            {var subQ0=sQuery(id+"F2.wireOp",EDGE,"E28.11.12.0");var subQ3=makeQuery(id+"F2.imprint","INTERSECT",VERTEX,{"derivedFrom":[sQuery(id+"F2.wireOp",EDGE,"E28.7.12.0"),subQ0]});Q40=makeQuery(id+"F2.imprint","IMPRINT",FACE,{"disambiguationData":[TD([[makeQuery(id+"F2.imprint","IMPRINT",EDGE,{"disambiguationData":[TD([[subQ3,-1.0]])],"derivedFrom":subQ0}),1.0]])]});}
            var Q41;
            {var subQ3=sQuery(id+"F2.wireOp",EDGE,"E28.14.12.0");Q41=makeQuery(id+"F2.imprint","IMPRINT",FACE,{"disambiguationData":[TD([[makeQuery(id+"F2.imprint","IMPRINT",EDGE,{"derivedFrom":subQ3}),-1.0]])]});}
            var Q42;
            {var subQ1=sQuery(id+"F2.wireOp",EDGE,"E28.2.11.0");Q42=makeQuery(id+"F2.imprint","IMPRINT",FACE,{"disambiguationData":[TD([[makeQuery(id+"F2.imprint","IMPRINT",EDGE,{"derivedFrom":subQ1}),1.0]])]});}
            var Q43;
            {var subQ3=sQuery(id+"F2.wireOp",EDGE,"E28.7.11.0");Q43=makeQuery(id+"F2.imprint","IMPRINT",FACE,{"disambiguationData":[TD([[makeQuery(id+"F2.imprint","IMPRINT",EDGE,{"derivedFrom":subQ3}),-1.0]])]});}
            var Q44;
            {var subQ0=sQuery(id+"F2.wireOp",EDGE,"E28.11.11.0");var subQ3=makeQuery(id+"F2.imprint","INTERSECT",VERTEX,{"derivedFrom":[sQuery(id+"F2.wireOp",EDGE,"E28.7.11.0"),subQ0]});Q44=makeQuery(id+"F2.imprint","IMPRINT",FACE,{"disambiguationData":[TD([[makeQuery(id+"F2.imprint","IMPRINT",EDGE,{"disambiguationData":[TD([[subQ3,-1.0]])],"derivedFrom":subQ0}),1.0]])]});}
            var Q45;
            {var subQ3=sQuery(id+"F2.wireOp",EDGE,"E28.7.10.0");Q45=makeQuery(id+"F2.imprint","IMPRINT",FACE,{"disambiguationData":[TD([[makeQuery(id+"F2.imprint","IMPRINT",EDGE,{"derivedFrom":subQ3}),-1.0]])]});}
            var Q46;
            {var subQ0=sQuery(id+"F2.wireOp",EDGE,"E28.11.10.0");var subQ3=makeQuery(id+"F2.imprint","INTERSECT",VERTEX,{"derivedFrom":[sQuery(id+"F2.wireOp",EDGE,"E28.7.10.0"),subQ0]});Q46=makeQuery(id+"F2.imprint","IMPRINT",FACE,{"disambiguationData":[TD([[makeQuery(id+"F2.imprint","IMPRINT",EDGE,{"disambiguationData":[TD([[subQ3,-1.0]])],"derivedFrom":subQ0}),1.0]])]});}
            var Q47;
            {var subQ3=sQuery(id+"F2.wireOp",EDGE,"E28.7.9.0");Q47=makeQuery(id+"F2.imprint","IMPRINT",FACE,{"disambiguationData":[TD([[makeQuery(id+"F2.imprint","IMPRINT",EDGE,{"derivedFrom":subQ3}),-1.0]])]});}
            var Q48;
            {var subQ0=sQuery(id+"F2.wireOp",EDGE,"E28.11.9.0");var subQ3=makeQuery(id+"F2.imprint","INTERSECT",VERTEX,{"derivedFrom":[sQuery(id+"F2.wireOp",EDGE,"E28.7.9.0"),subQ0]});Q48=makeQuery(id+"F2.imprint","IMPRINT",FACE,{"disambiguationData":[TD([[makeQuery(id+"F2.imprint","IMPRINT",EDGE,{"disambiguationData":[TD([[subQ3,-1.0]])],"derivedFrom":subQ0}),1.0]])]});}
            var Q49;
            {var subQ3=sQuery(id+"F2.wireOp",EDGE,"E28.14.9.0");Q49=makeQuery(id+"F2.imprint","IMPRINT",FACE,{"disambiguationData":[TD([[makeQuery(id+"F2.imprint","IMPRINT",EDGE,{"derivedFrom":subQ3}),-1.0]])]});}
            var Q50;
            {var subQ1=sQuery(id+"F2.wireOp",EDGE,"E28.2.8.0");Q50=makeQuery(id+"F2.imprint","IMPRINT",FACE,{"disambiguationData":[TD([[makeQuery(id+"F2.imprint","IMPRINT",EDGE,{"derivedFrom":subQ1}),1.0]])]});}
            var Q51;
            {var subQ1=sQuery(id+"F2.wireOp",EDGE,"E28.2.9.0");Q51=makeQuery(id+"F2.imprint","IMPRINT",FACE,{"disambiguationData":[TD([[makeQuery(id+"F2.imprint","IMPRINT",EDGE,{"derivedFrom":subQ1}),1.0]])]});}
            var Q52;
            {var subQ1=sQuery(id+"F2.wireOp",EDGE,"E28.2.10.0");Q52=makeQuery(id+"F2.imprint","IMPRINT",FACE,{"disambiguationData":[TD([[makeQuery(id+"F2.imprint","IMPRINT",EDGE,{"derivedFrom":subQ1}),1.0]])]});}
            var Q53;
            {var subQ3=sQuery(id+"F2.wireOp",EDGE,"E28.14.10.0");Q53=makeQuery(id+"F2.imprint","IMPRINT",FACE,{"disambiguationData":[TD([[makeQuery(id+"F2.imprint","IMPRINT",EDGE,{"derivedFrom":subQ3}),-1.0]])]});}
            var Q54;
            {var subQ3=sQuery(id+"F2.wireOp",EDGE,"E28.14.11.0");Q54=makeQuery(id+"F2.imprint","IMPRINT",FACE,{"disambiguationData":[TD([[makeQuery(id+"F2.imprint","IMPRINT",EDGE,{"derivedFrom":subQ3}),-1.0]])]});}
            var Q55;
            {var subQ3=sQuery(id+"F2.wireOp",EDGE,"E28.7.8.0");Q55=makeQuery(id+"F2.imprint","IMPRINT",FACE,{"disambiguationData":[TD([[makeQuery(id+"F2.imprint","IMPRINT",EDGE,{"derivedFrom":subQ3}),-1.0]])]});}
            var Q56;
            {var subQ0=sQuery(id+"F2.wireOp",EDGE,"E28.11.8.0");var subQ3=makeQuery(id+"F2.imprint","INTERSECT",VERTEX,{"derivedFrom":[sQuery(id+"F2.wireOp",EDGE,"E28.7.8.0"),subQ0]});Q56=makeQuery(id+"F2.imprint","IMPRINT",FACE,{"disambiguationData":[TD([[makeQuery(id+"F2.imprint","IMPRINT",EDGE,{"disambiguationData":[TD([[subQ3,-1.0]])],"derivedFrom":subQ0}),1.0]])]});}
            var Q57;
            {var subQ3=sQuery(id+"F2.wireOp",EDGE,"E28.14.8.0");Q57=makeQuery(id+"F2.imprint","IMPRINT",FACE,{"disambiguationData":[TD([[makeQuery(id+"F2.imprint","IMPRINT",EDGE,{"derivedFrom":subQ3}),-1.0]])]});}
            var Q58;
            {var subQ1=sQuery(id+"F2.wireOp",EDGE,"E27.2.7.0");Q58=makeQuery(id+"F2.imprint","IMPRINT",FACE,{"disambiguationData":[TD([[makeQuery(id+"F2.imprint","IMPRINT",EDGE,{"derivedFrom":subQ1}),1.0]])]});}
            var Q59;
            {var subQ4=sQuery(id+"F2.wireOp",EDGE,"E28.2.13.0");Q59=makeQuery(id+"F2.imprint","IMPRINT",FACE,{"disambiguationData":[TD([[makeQuery(id+"F2.imprint","IMPRINT",EDGE,{"derivedFrom":subQ4}),1.0]])]});}
            var Q60;
            {var subQ3=sQuery(id+"F2.wireOp",EDGE,"E29.14.14.0");Q60=makeQuery(id+"F2.imprint","IMPRINT",FACE,{"disambiguationData":[TD([[makeQuery(id+"F2.imprint","IMPRINT",EDGE,{"derivedFrom":subQ3}),-1.0]])]});}
            var Q61;
            {var subQ0=sQuery(id+"F2.wireOp",EDGE,"E29.11.14.0");var subQ3=makeQuery(id+"F2.imprint","INTERSECT",VERTEX,{"derivedFrom":[sQuery(id+"F2.wireOp",EDGE,"E29.7.14.0"),subQ0]});Q61=makeQuery(id+"F2.imprint","IMPRINT",FACE,{"disambiguationData":[TD([[makeQuery(id+"F2.imprint","IMPRINT",EDGE,{"disambiguationData":[TD([[subQ3,-1.0]])],"derivedFrom":subQ0}),1.0]])]});}
            var Q62;
            {var subQ3=sQuery(id+"F2.wireOp",EDGE,"E29.7.14.0");Q62=makeQuery(id+"F2.imprint","IMPRINT",FACE,{"disambiguationData":[TD([[makeQuery(id+"F2.imprint","IMPRINT",EDGE,{"derivedFrom":subQ3}),-1.0]])]});}
            var Q63;
            {var subQ1=sQuery(id+"F2.wireOp",EDGE,"E29.2.14.0");Q63=makeQuery(id+"F2.imprint","IMPRINT",FACE,{"disambiguationData":[TD([[makeQuery(id+"F2.imprint","IMPRINT",EDGE,{"derivedFrom":subQ1}),1.0]])]});}
            var Q64;
            {var subQ0=sQuery(id+"F2.wireOp",EDGE,"E29.11.15.0");var subQ3=makeQuery(id+"F2.imprint","INTERSECT",VERTEX,{"derivedFrom":[sQuery(id+"F2.wireOp",EDGE,"E29.7.15.0"),subQ0]});Q64=makeQuery(id+"F2.imprint","IMPRINT",FACE,{"disambiguationData":[TD([[makeQuery(id+"F2.imprint","IMPRINT",EDGE,{"disambiguationData":[TD([[subQ3,-1.0]])],"derivedFrom":subQ0}),1.0]])]});}
            var Q65;
            {var subQ3=sQuery(id+"F2.wireOp",EDGE,"E29.7.15.0");Q65=makeQuery(id+"F2.imprint","IMPRINT",FACE,{"disambiguationData":[TD([[makeQuery(id+"F2.imprint","IMPRINT",EDGE,{"derivedFrom":subQ3}),-1.0]])]});}
            var Q66;
            {var subQ3=sQuery(id+"F2.wireOp",EDGE,"E29.14.15.0");Q66=makeQuery(id+"F2.imprint","IMPRINT",FACE,{"disambiguationData":[TD([[makeQuery(id+"F2.imprint","IMPRINT",EDGE,{"derivedFrom":subQ3}),-1.0]])]});}
            var Q67;
            {var subQ4=sQuery(id+"F2.wireOp",EDGE,"E29.2.15.0");Q67=makeQuery(id+"F2.imprint","IMPRINT",FACE,{"disambiguationData":[TD([[makeQuery(id+"F2.imprint","IMPRINT",EDGE,{"derivedFrom":subQ4}),1.0]])]});}
            var Q68;
            {var subQ3=sQuery(id+"F2.wireOp",EDGE,"E30.14.16.0");Q68=makeQuery(id+"F2.imprint","IMPRINT",FACE,{"disambiguationData":[TD([[makeQuery(id+"F2.imprint","IMPRINT",EDGE,{"derivedFrom":subQ3}),-1.0]])]});}
            var Q69;
            {var subQ0=sQuery(id+"F2.wireOp",EDGE,"E30.11.16.0");var subQ3=makeQuery(id+"F2.imprint","INTERSECT",VERTEX,{"derivedFrom":[sQuery(id+"F2.wireOp",EDGE,"E30.7.16.0"),subQ0]});Q69=makeQuery(id+"F2.imprint","IMPRINT",FACE,{"disambiguationData":[TD([[makeQuery(id+"F2.imprint","IMPRINT",EDGE,{"disambiguationData":[TD([[subQ3,-1.0]])],"derivedFrom":subQ0}),1.0]])]});}
            var Q70;
            {var subQ3=sQuery(id+"F2.wireOp",EDGE,"E30.7.16.0");Q70=makeQuery(id+"F2.imprint","IMPRINT",FACE,{"disambiguationData":[TD([[makeQuery(id+"F2.imprint","IMPRINT",EDGE,{"derivedFrom":subQ3}),-1.0]])]});}
            var Q71;
            {var subQ1=sQuery(id+"F2.wireOp",EDGE,"E30.2.16.0");Q71=makeQuery(id+"F2.imprint","IMPRINT",FACE,{"disambiguationData":[TD([[makeQuery(id+"F2.imprint","IMPRINT",EDGE,{"derivedFrom":subQ1}),1.0]])]});}
            var Q72;
            {var subQ0=sQuery(id+"F2.wireOp",EDGE,"E30.11.17.0");var subQ3=makeQuery(id+"F2.imprint","INTERSECT",VERTEX,{"derivedFrom":[sQuery(id+"F2.wireOp",EDGE,"E30.7.17.0"),subQ0]});Q72=makeQuery(id+"F2.imprint","IMPRINT",FACE,{"disambiguationData":[TD([[makeQuery(id+"F2.imprint","IMPRINT",EDGE,{"disambiguationData":[TD([[subQ3,-1.0]])],"derivedFrom":subQ0}),1.0]])]});}
            var Q73;
            {var subQ3=sQuery(id+"F2.wireOp",EDGE,"E30.14.17.0");Q73=makeQuery(id+"F2.imprint","IMPRINT",FACE,{"disambiguationData":[TD([[makeQuery(id+"F2.imprint","IMPRINT",EDGE,{"derivedFrom":subQ3}),-1.0]])]});}
            var Q74;
            {var subQ3=sQuery(id+"F2.wireOp",EDGE,"E30.7.17.0");Q74=makeQuery(id+"F2.imprint","IMPRINT",FACE,{"disambiguationData":[TD([[makeQuery(id+"F2.imprint","IMPRINT",EDGE,{"derivedFrom":subQ3}),-1.0]])]});}
            var Q75;
            {var subQ1=sQuery(id+"F2.wireOp",EDGE,"E30.2.17.0");Q75=makeQuery(id+"F2.imprint","IMPRINT",FACE,{"disambiguationData":[TD([[makeQuery(id+"F2.imprint","IMPRINT",EDGE,{"derivedFrom":subQ1}),1.0]])]});}
            var Q76;
            {var subQ0=sQuery(id+"F2.wireOp",EDGE,"E30.11.18.0");var subQ3=makeQuery(id+"F2.imprint","INTERSECT",VERTEX,{"derivedFrom":[sQuery(id+"F2.wireOp",EDGE,"E30.7.18.0"),subQ0]});Q76=makeQuery(id+"F2.imprint","IMPRINT",FACE,{"disambiguationData":[TD([[makeQuery(id+"F2.imprint","IMPRINT",EDGE,{"disambiguationData":[TD([[subQ3,-1.0]])],"derivedFrom":subQ0}),1.0]])]});}
            var Q77;
            {var subQ3=sQuery(id+"F2.wireOp",EDGE,"E30.14.18.0");Q77=makeQuery(id+"F2.imprint","IMPRINT",FACE,{"disambiguationData":[TD([[makeQuery(id+"F2.imprint","IMPRINT",EDGE,{"derivedFrom":subQ3}),-1.0]])]});}
            var Q78;
            {var subQ0=sQuery(id+"F2.wireOp",EDGE,"E30.11.19.0");var subQ3=makeQuery(id+"F2.imprint","INTERSECT",VERTEX,{"derivedFrom":[sQuery(id+"F2.wireOp",EDGE,"E30.7.19.0"),subQ0]});Q78=makeQuery(id+"F2.imprint","IMPRINT",FACE,{"disambiguationData":[TD([[makeQuery(id+"F2.imprint","IMPRINT",EDGE,{"disambiguationData":[TD([[subQ3,-1.0]])],"derivedFrom":subQ0}),1.0]])]});}
            var Q79;
            {var subQ3=sQuery(id+"F2.wireOp",EDGE,"E30.14.19.0");Q79=makeQuery(id+"F2.imprint","IMPRINT",FACE,{"disambiguationData":[TD([[makeQuery(id+"F2.imprint","IMPRINT",EDGE,{"derivedFrom":subQ3}),-1.0]])]});}
            var Q80;
            {var subQ3=sQuery(id+"F2.wireOp",EDGE,"E30.7.19.0");Q80=makeQuery(id+"F2.imprint","IMPRINT",FACE,{"disambiguationData":[TD([[makeQuery(id+"F2.imprint","IMPRINT",EDGE,{"derivedFrom":subQ3}),-1.0]])]});}
            var Q81;
            {var subQ1=sQuery(id+"F2.wireOp",EDGE,"E30.2.18.0");Q81=makeQuery(id+"F2.imprint","IMPRINT",FACE,{"disambiguationData":[TD([[makeQuery(id+"F2.imprint","IMPRINT",EDGE,{"derivedFrom":subQ1}),1.0]])]});}
            var Q82;
            {var subQ3=sQuery(id+"F2.wireOp",EDGE,"E30.7.18.0");Q82=makeQuery(id+"F2.imprint","IMPRINT",FACE,{"disambiguationData":[TD([[makeQuery(id+"F2.imprint","IMPRINT",EDGE,{"derivedFrom":subQ3}),-1.0]])]});}
            extrude(context, id + "F3", {"entities" : qUnion([Q0, Q1, Q2, Q3, Q4, Q5, Q6, Q7, Q8, Q9, Q10, Q11, Q12, Q13, Q14, Q15, Q16, Q17, Q18, Q19, Q20, Q21, Q22, Q23, Q24, Q25, Q26, Q27, Q28, Q29, Q30, Q31, Q32, Q33, Q34, Q35, Q36, Q37, Q38, Q39, Q40, Q41, Q42, Q43, Q44, Q45, Q46, Q47, Q48, Q49, Q50, Q51, Q52, Q53, Q54, Q55, Q56, Q57, Q58, Q59, Q60, Q61, Q62, Q63, Q64, Q65, Q66, Q67, Q68, Q69, Q70, Q71, Q72, Q73, Q74, Q75, Q76, Q77, Q78, Q79, Q80, Q81, Q82]), "operationType" : NewBodyOperationType.REMOVE, "oppositeDirection" : true, "depth" : 25 * mm, "offsetDistance" : 25 * mm});
        }
        {
            var Q0;
            Q0=makeQuery(id+"F1.opRevolve","SWEPT_FACE",FACE,{"disambiguationData":[OSD([sQuery(id+"F0.wireOp",EDGE,"E0.top")])]});
            var sketch = newSketch(context, id + "F4", { "sketchPlane" : qUnion([Q0])});
            skCircle(sketch, "E31", {"center": v(0, 0) * mm, "radius": 1.13 * mm});
            skCircle(sketch, "E32", {"center": v(0, 0) * mm, "radius": 1.38 * mm});
            skSolve(sketch);
        }
        {
            var Q0;
            Q0=makeQuery(id+"F1.opRevolve","SWEPT_FACE",FACE,{"disambiguationData":[OSD([sQuery(id+"F0.wireOp",EDGE,"E0.bottom")])]});
            var sketch = newSketch(context, id + "F5", { "sketchPlane" : qUnion([Q0])});
            skCircle(sketch, "E33.0", {"center": v(0, 0) * mm, "radius": 1.38 * mm});
            skCircle(sketch, "E34.0", {"center": v(0, 0) * mm, "radius": 1.13 * mm});
            skSolve(sketch);
        }
        {
            var Q0;
            Q0=makeQuery(id+"F5.imprint","IMPRINT",FACE,{"disambiguationData":[TD([[makeQuery(id+"F5.imprint","IMPRINT",EDGE,{"derivedFrom":sQuery(id+"F5.wireOp",EDGE,"E33.0")}),-1.0]])]});
            extrude(context, id + "F6", {"entities" : qUnion([Q0]), "operationType" : NewBodyOperationType.REMOVE, "oppositeDirection" : true, "depth" : 0.5 * mm, "offsetDistance" : 25 * mm});
        }
        {
            var Q0;
            Q0=makeQuery(id+"F4.imprint","IMPRINT",FACE,{"disambiguationData":[TD([[makeQuery(id+"F4.imprint","IMPRINT",EDGE,{"derivedFrom":sQuery(id+"F4.wireOp",EDGE,"E31")}),-1.0]])]});
            extrude(context, id + "F7", {"entities" : qUnion([Q0]), "operationType" : NewBodyOperationType.REMOVE, "surfaceOperationType" : NewSurfaceOperationType.ADD, "oppositeDirection" : true, "depth" : 0.5 * mm, "offsetDistance" : 25 * mm});
        }
    });
